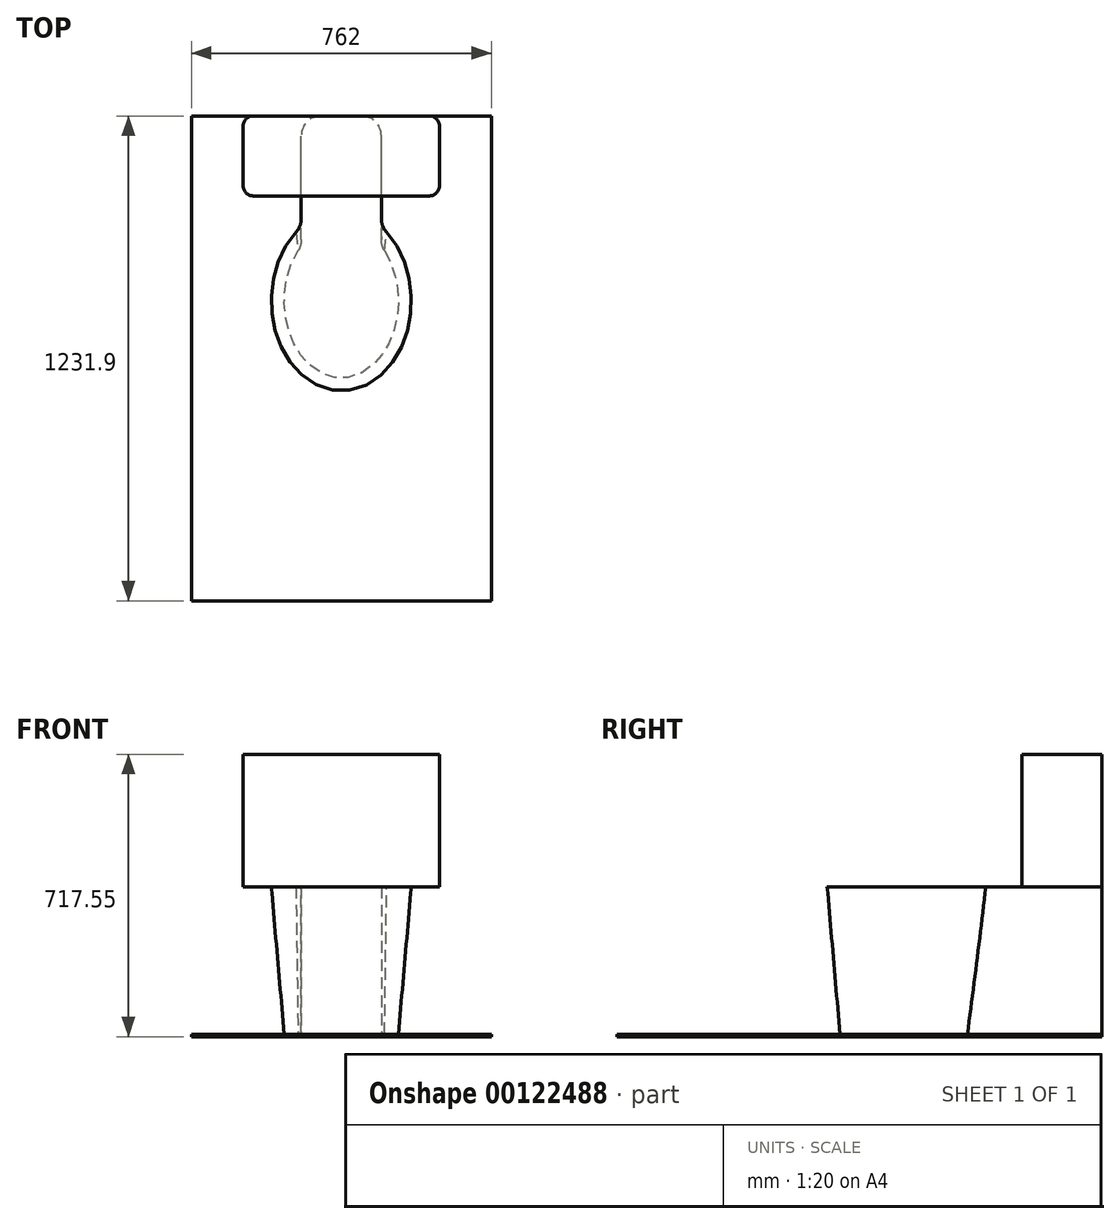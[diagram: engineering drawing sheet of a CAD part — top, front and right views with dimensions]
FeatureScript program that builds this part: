
annotation { "Feature Type Name" : "Feature", "Feature Type Description" : "" }
export const myFeature = defineFeature(function(context is Context, id is Id, definition is map)
    precondition{}
    {
        {
            var Q0;
            Q0=qCreatedBy(makeId("Top.planeOp"),FACE);
            cPlane(context, id + "F0", {"entities" : qUnion([Q0]), "cplaneType" : CPlaneType.OFFSET, "offset" : 381 * mm, "width" : 152.4 * mm, "height" : 152.4 * mm});
        }
        {
            var Q0;
            Q0=qCreatedBy(makeId("Top.planeOp"),FACE);
            cPlane(context, id + "F1", {"entities" : qUnion([Q0]), "cplaneType" : CPlaneType.OFFSET, "offset" : 717.55 * mm, "width" : 152.4 * mm, "height" : 152.4 * mm});
        }
        {
            var Q0;
            Q0=qCreatedBy(id+"F0.planeOp",FACE);
            var sketch = newSketch(context, id + "F2", { "sketchPlane" : qUnion([Q0])});
            skEllipse(sketch, "E0", {"center": v(0, 0) * mm, "majorRadius": 228.6 * mm, "minorRadius": 177.8 * mm, "majorAxis": v(0, 1)});
            skSolve(sketch);
        }
        {
            var Q0;
            Q0=qCreatedBy(makeId("Top.planeOp"),FACE);
            var sketch = newSketch(context, id + "F3", { "sketchPlane" : qUnion([Q0])});
            skLineSegment(sketch, "E1.bottom", {"start": v(-101.6, 0) * mm, "end": v(101.6, 0) * mm});
            skLineSegment(sketch, "E1.top", {"start": v(-101.6, 469.9) * mm, "end": v(101.6, 469.9) * mm});
            skLineSegment(sketch, "E1.left", {"start": v(-101.6, 0) * mm, "end": v(-101.6, 469.9) * mm});
            skLineSegment(sketch, "E1.right", {"start": v(101.6, 0) * mm, "end": v(101.6, 469.9) * mm});
            skLineSegment(sketch, "E2", {"start": v(0, 0) * mm, "end": v(0, -228.6) * mm});
            skSolve(sketch);
        }
        {
            var Q0;
            Q0=qCreatedBy(id+"F0.planeOp",FACE);
            var sketch = newSketch(context, id + "F4", { "sketchPlane" : qUnion([Q0])});
            skLineSegment(sketch, "E3.bottom", {"start": v(-249.24, 469.9) * mm, "end": v(249.24, 469.9) * mm});
            skLineSegment(sketch, "E3.top", {"start": v(-249.24, 266.7) * mm, "end": v(249.24, 266.7) * mm});
            skLineSegment(sketch, "E3.left", {"start": v(-249.24, 469.9) * mm, "end": v(-249.24, 266.7) * mm});
            skLineSegment(sketch, "E3.right", {"start": v(249.24, 469.9) * mm, "end": v(249.24, 266.7) * mm});
            skLineSegment(sketch, "E4", {"start": v(0, 266.7) * mm, "end": v(0, 0) * mm, "construction": true});
            skSolve(sketch);
        }
        {
            var Q0;
            Q0=qCreatedBy(makeId("Top.planeOp"),FACE);
            var sketch = newSketch(context, id + "F5", { "sketchPlane" : qUnion([Q0])});
            skLineSegment(sketch, "E5.bottom", {"start": v(-381, -762) * mm, "end": v(381, -762) * mm});
            skLineSegment(sketch, "E5.top", {"start": v(-381, 469.9) * mm, "end": v(381, 469.9) * mm});
            skLineSegment(sketch, "E5.left", {"start": v(-381, -762) * mm, "end": v(-381, 469.9) * mm});
            skLineSegment(sketch, "E5.right", {"start": v(381, -762) * mm, "end": v(381, 469.9) * mm});
            skSolve(sketch);
        }
        {
            var Q0;
            Q0 = qSketchRegion(id + "F2", true);
            var Q1;
            Q1=qCreatedBy(makeId("Top.planeOp"),FACE);
            extrude(context, id + "F6", {"entities" : qUnion([Q0]), "endBound" : BoundingType.UP_TO_SURFACE, "oppositeDirection" : true, "endBoundEntityFace" : qUnion([Q1]), "depth" : 25.4 * mm, "hasDraft" : true, "draftAngle" : 5 * degree, "draftPullDirection" : true});
        }
        {
            var Q0;
            Q0 = qSketchRegion(id + "F3", true);
            var Q1;
            Q1=qCreatedBy(id+"F0.planeOp",FACE);
            extrude(context, id + "F7", {"entities" : qUnion([Q0]), "operationType" : NewBodyOperationType.ADD, "endBound" : BoundingType.UP_TO_SURFACE, "endBoundEntityFace" : qUnion([Q1]), "depth" : 25.4 * mm});
        }
        {
            var Q0;
            Q0 = qSketchRegion(id + "F4", true);
            var Q1;
            Q1=qCreatedBy(id+"F1.planeOp",FACE);
            extrude(context, id + "F8", {"entities" : qUnion([Q0]), "operationType" : NewBodyOperationType.ADD, "endBound" : BoundingType.UP_TO_SURFACE, "endBoundEntityFace" : qUnion([Q1]), "depth" : 25.4 * mm});
        }
        {
            var Q0;
            Q0=makeQuery(id+"F7.opExtrude","SWEPT_EDGE",EDGE,{"disambiguationData":[OSD([sQuery(id+"F3.wireOp",EDGE,"E1.top"),sQuery(id+"F3.wireOp",EDGE,"E1.left")])]});
            var Q1;
            Q1=makeQuery(id+"F7.opExtrude","SWEPT_EDGE",EDGE,{"disambiguationData":[OSD([sQuery(id+"F3.wireOp",EDGE,"E1.top"),sQuery(id+"F3.wireOp",EDGE,"E1.right")])]});
            fillet(context, id + "F9", {"entities" : qUnion([Q0, Q1]), "radius" : 50.8 * mm, "tangentPropagation" : true, "allowEdgeOverflow" : false});
        }
        {
            var Q0;
            Q0=makeQuery(id+"F7.boolean.opBoolean","INTERSECT",EDGE,{"derivedFrom":[makeQuery(id+"F6.opExtrude","SWEPT_FACE",FACE,{"disambiguationData":[OSD([sQuery(id+"F2.wireOp",EDGE,"E0")])]}),makeQuery(id+"F7.opExtrude","SWEPT_FACE",FACE,{"disambiguationData":[OSD([sQuery(id+"F3.wireOp",EDGE,"E1.left")])]})]});
            var Q1;
            Q1=makeQuery(id+"F7.boolean.opBoolean","INTERSECT",EDGE,{"derivedFrom":[makeQuery(id+"F6.opExtrude","SWEPT_FACE",FACE,{"disambiguationData":[OSD([sQuery(id+"F2.wireOp",EDGE,"E0")])]}),makeQuery(id+"F7.opExtrude","SWEPT_FACE",FACE,{"disambiguationData":[OSD([sQuery(id+"F3.wireOp",EDGE,"E1.right")])]})]});
            fillet(context, id + "F10", {"entities" : qUnion([Q0, Q1]), "radius" : 50.8 * mm, "tangentPropagation" : true, "allowEdgeOverflow" : false});
        }
        {
            var Q0;
            Q0=makeQuery(id+"F8.opExtrude","SWEPT_EDGE",EDGE,{"disambiguationData":[OSD([sQuery(id+"F4.wireOp",EDGE,"E3.top"),sQuery(id+"F4.wireOp",EDGE,"E3.right")])]});
            var Q1;
            Q1=makeQuery(id+"F8.opExtrude","SWEPT_EDGE",EDGE,{"disambiguationData":[OSD([sQuery(id+"F4.wireOp",EDGE,"E3.bottom"),sQuery(id+"F4.wireOp",EDGE,"E3.right")])]});
            var Q2;
            Q2=makeQuery(id+"F8.opExtrude","SWEPT_EDGE",EDGE,{"disambiguationData":[OSD([sQuery(id+"F4.wireOp",EDGE,"E3.top"),sQuery(id+"F4.wireOp",EDGE,"E3.left")])]});
            var Q3;
            Q3=makeQuery(id+"F8.opExtrude","SWEPT_EDGE",EDGE,{"disambiguationData":[OSD([sQuery(id+"F4.wireOp",EDGE,"E3.bottom"),sQuery(id+"F4.wireOp",EDGE,"E3.left")])]});
            fillet(context, id + "F11", {"entities" : qUnion([Q0, Q1, Q2, Q3]), "radius" : 25.4 * mm, "tangentPropagation" : true, "allowEdgeOverflow" : false});
        }
        {
            var Q0;
            Q0 = qSketchRegion(id + "F5", true);
            extrude(context, id + "F12", {"entities" : qUnion([Q0]), "operationType" : NewBodyOperationType.ADD, "depth" : 6.35 * mm});
        }
    });
